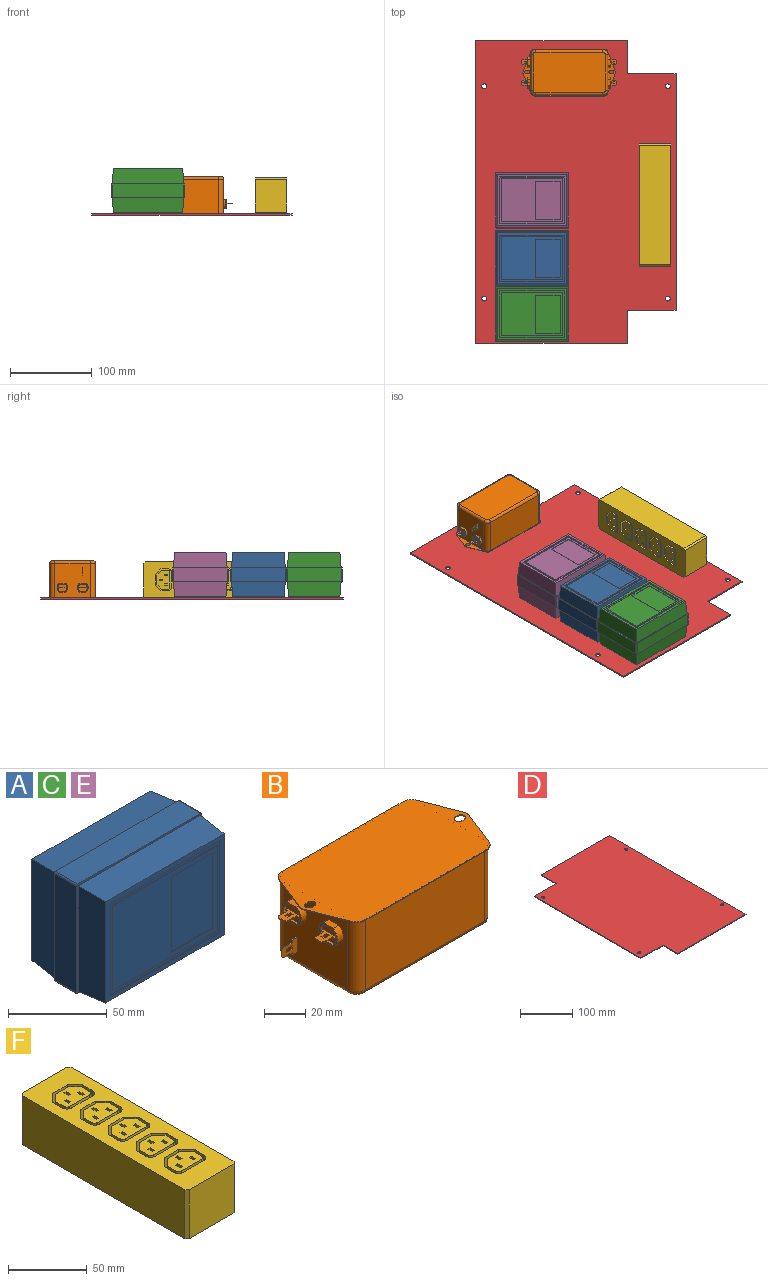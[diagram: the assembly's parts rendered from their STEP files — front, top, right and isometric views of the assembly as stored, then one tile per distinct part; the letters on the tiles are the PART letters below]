
ASSEMBLY  parts=6 mates=7
PART A: 47 faces, bbox 90x55x68 mm
  f0: plane 84.83x62.83mm, normal (0,-1,0), area 849.9mm2, adj f1,f2,f3,f4,f35,f36,f37,f38
  f1: plane 65.74x18.5mm, normal (-1,-0.08,0), area 1192.9mm2, adj f0,f2,f4,f9
  f2: plane 87.74x18.5mm, normal (0,-0.08,-1), area 1601.2mm2, adj f0,f1,f3,f9
  f3: plane 65.74x18.5mm, normal (1,-0.08,0), area 1192.9mm2, adj f0,f2,f4,f9
  f4: plane 87.74x18.5mm, normal (0,-0.08,1), area 1601.2mm2, adj f0,f1,f3,f9
  f5: plane 66x16mm, normal (-1,0,0), area 1056mm2, adj f9,f10,f16,f19
  f6: plane 88x16mm, normal (0,0,-1), area 1408mm2, adj f9,f10,f16,f17
  f7: plane 66x16mm, normal (1,0,0), area 1056mm2, adj f9,f10,f17,f18
  f8: plane 88x16mm, normal (0,0,1), area 1408mm2, adj f9,f10,f18,f19
  f9: plane 90x68mm, normal (0,-1,0), area 351mm2, adj f1,f2,f3,f4,f5,f6,f7,f8
  f10: plane 90x68mm, normal (0,1,0), area 351mm2, adj f5,f6,f7,f8,f12,f13,f14,f15
  f11: plane 84.83x62.83mm, normal (0,1,0), area 5128.6mm2, adj f12,f13,f14,f15,f20,f22,f24,f26
  f12: plane 65.74x18.5mm, normal (-1,0.08,0), area 1192.9mm2, adj f10,f11,f13,f15
  f13: plane 87.74x18.5mm, normal (0,0.08,-1), area 1601.2mm2, adj f10,f11,f12,f14
  f14: plane 65.74x18.5mm, normal (1,0.08,0), area 1192.9mm2, adj f10,f11,f13,f15
  f15: plane 87.74x18.5mm, normal (0,0.08,1), area 1601.2mm2, adj f10,f11,f12,f14
  f16: cylinder r=1mm len=16mm, axis (0,-1,0), area 25.1mm2, adj f5,f6,f9,f10
  f17: cylinder r=1mm len=16mm, axis (0,1,0), area 25.1mm2, adj f6,f7,f9,f10
  f18: cylinder r=1mm len=16mm, axis (0,-1,0), area 25.1mm2, adj f7,f8,f9,f10
  f19: cylinder r=1mm len=16mm, axis (0,1,0), area 25.1mm2, adj f5,f8,f9,f10
  f20: cylinder r=4mm len=8mm, axis (0,-1,0), area 36.7mm2, adj f11,f31
  f21: plane 6.92x6.92mm, normal (0,1,0), area 37.6mm2, adj f31
  f22: cylinder r=4mm len=8mm, axis (0,-1,0), area 36.7mm2, adj f11,f30
  f23: plane 6.92x6.92mm, normal (0,1,0), area 37.6mm2, adj f30
  f24: cylinder r=4mm len=8mm, axis (0,-1,0), area 36.7mm2, adj f11,f29
  f25: plane 6.92x6.92mm, normal (0,1,0), area 37.6mm2, adj f29
  f26: cylinder r=4mm len=8mm, axis (0,-1,0), area 36.7mm2, adj f11,f28
  f27: plane 6.92x6.92mm, normal (0,1,0), area 37.6mm2, adj f28
  f28: cone r=3.46mm half-angle=45deg, axis (0,-1,0), area 17.9mm2, adj f26,f27
  f29: cone r=3.46mm half-angle=45deg, axis (0,-1,0), area 17.9mm2, adj f24,f25
  f30: cone r=3.46mm half-angle=45deg, axis (0,-1,0), area 17.9mm2, adj f22,f23
  f31: cone r=3.46mm half-angle=45deg, axis (0,-1,0), area 17.9mm2, adj f20,f21
  f32: plane 52.83x0.5mm, normal (-1,0,0), area 26.4mm2, adj f33,f39,f40,f41
  f33: plane 74.83x0.5mm, normal (0,0,1), area 37.4mm2, adj f32,f34,f40,f41
  f34: plane 52.83x0.5mm, normal (1,0,0), area 26.4mm2, adj f33,f39,f40,f41
  f35: plane 78.83x0.5mm, normal (0,0,1), area 39.4mm2, adj f0,f36,f38,f40
  f36: plane 56.83x0.5mm, normal (-1,0,0), area 28.4mm2, adj f0,f35,f37,f40
  f37: plane 78.83x0.5mm, normal (0,0,-1), area 39.4mm2, adj f0,f36,f38,f40
  f38: plane 56.83x0.5mm, normal (1,0,0), area 28.4mm2, adj f0,f35,f37,f40
  f39: plane 74.83x0.5mm, normal (0,0,-1), area 37.4mm2, adj f32,f34,f40,f41
  f40: plane 78.83x56.83mm, normal (0,-1,0), area 526.6mm2, adj f32,f33,f34,f35,f36,f37,f38,f39
  f41: plane 74.83x52.83mm, normal (0,-1,0), area 2548.3mm2, adj f32,f33,f34,f39,f42,f43,f44,f45
  f42: plane 46.83x0.5mm, normal (-1,0,0), area 23.4mm2, adj f41,f43,f45,f46
  f43: plane 30x0.5mm, normal (0,0,-1), area 15mm2, adj f41,f42,f44,f46
  f44: plane 46.83x0.5mm, normal (1,0,0), area 23.4mm2, adj f41,f43,f45,f46
  f45: plane 30x0.5mm, normal (0,0,1), area 15mm2, adj f41,f42,f44,f46
  f46: plane 46.83x30mm, normal (0,-1,0), area 1404.9mm2, adj f42,f43,f44,f45
PART B: 154 faces, bbox 116x57.5x45.4 mm
  f0: plane 1.5x0.5mm, normal (0,-1,0), area 0.8mm2, adj f6,f7,f128,f148
  f1: plane 1.5x0.5mm, normal (0,1,0), area 0.8mm2, adj f6,f7,f128,f146
  f2: plane 4x0.5mm, normal (1,0,0), area 2mm2, adj f6,f7,f152,f153
  f3: plane 1.5x0.5mm, normal (0,-1,0), area 0.8mm2, adj f8,f9,f133,f145
  f4: plane 1.5x0.5mm, normal (0,1,0), area 0.8mm2, adj f8,f9,f133,f143
  f5: plane 4x0.5mm, normal (1,0,0), area 2mm2, adj f8,f9,f150,f151
  f6: plane 9x8.5mm, normal (0,0,1), area 46.5mm2, adj f0,f1,f2,f128,f138,f139,f140,f141
  f7: plane 9x8.5mm, normal (0,0,-1), area 46.5mm2, adj f0,f1,f2,f128,f138,f139,f140,f141
  f8: plane 9x8.5mm, normal (0,0,1), area 46.5mm2, adj f3,f4,f5,f133,f134,f135,f136,f137
  f9: plane 9x8.5mm, normal (0,0,-1), area 46.5mm2, adj f3,f4,f5,f133,f134,f135,f136,f137
  f10: plane 13x11mm, normal (1,0,0), area 36.9mm2, adj f115,f116,f117,f118,f129,f130,f131,f132
  f11: plane 44x42mm, normal (1,0,0), area 1601.3mm2, adj f22,f44,f49,f57,f115,f116,f117,f118
  f12: plane 4x0.5mm, normal (-1,0,0), area 2mm2, adj f13,f14,f109,f110
  f13: plane 11x9mm, normal (0,1,0), area 69mm2, adj f12,f21,f83,f84,f101,f102,f103,f104
  f14: plane 11x9mm, normal (0,-1,0), area 69mm2, adj f12,f21,f83,f84,f101,f102,f103,f104
  f15: plane 4x0.5mm, normal (-1,0,0), area 2mm2, adj f17,f18,f113,f114
  f16: plane 4x0.5mm, normal (-1,0,0), area 2mm2, adj f19,f20,f111,f112
  f17: plane 9x8.5mm, normal (0,0,1), area 46.5mm2, adj f15,f73,f79,f80,f89,f90,f91,f92
  f18: plane 9x8.5mm, normal (0,0,-1), area 46.5mm2, adj f15,f73,f79,f80,f89,f90,f91,f92
  f19: plane 9x8.5mm, normal (0,0,1), area 46.5mm2, adj f16,f78,f81,f82,f85,f86,f87,f88
  f20: plane 9x8.5mm, normal (0,0,-1), area 46.5mm2, adj f16,f78,f81,f82,f85,f86,f87,f88
  f21: plane 44x42mm, normal (-1,0,0), area 1596.8mm2, adj f13,f14,f22,f46,f47,f52,f59,f60
  f22: plane 113.52x57.5mm, normal (0,0,-1), area 628.3mm2, adj f11,f21,f24,f25,f26,f27,f28,f29
  f23: plane 113.52x57.5mm, normal (0,0,1), area 5861.4mm2, adj f24,f25,f26,f27,f28,f29,f30,f31
  f24: cylinder r=4.4mm len=3.2mm, axis (0,0,-1), area 1.3mm2, adj f22,f23,f25,f35
  f25: plane 23.33x9.12mm, normal (-0.93,-0.36,0), area 10mm2, adj f22,f23,f24,f26
  f26: cylinder r=6mm len=5.5mm, axis (0,0,-1), area 2.8mm2, adj f22,f23,f25,f27
  f27: plane 83.68x0.4mm, normal (0,-1,0), area 33.5mm2, adj f22,f23,f26,f28
  f28: cylinder r=6mm len=5.5mm, axis (0,0,-1), area 2.8mm2, adj f22,f23,f27,f29
  f29: plane 23.33x9.12mm, normal (0.93,-0.36,0), area 10mm2, adj f22,f23,f28,f30
  f30: cylinder r=4.4mm len=3.2mm, axis (0,0,-1), area 1.3mm2, adj f22,f23,f29,f31
  f31: plane 23.33x9.12mm, normal (0.93,0.36,0), area 10mm2, adj f22,f23,f30,f32
  f32: cylinder r=6mm len=5.5mm, axis (0,0,-1), area 2.8mm2, adj f22,f23,f31,f33
  f33: plane 83.68x0.4mm, normal (0,1,0), area 33.5mm2, adj f22,f23,f32,f34
  f34: cylinder r=6mm len=5.5mm, axis (0,0,-1), area 2.8mm2, adj f22,f23,f33,f35
  f35: plane 23.33x9.12mm, normal (-0.93,0.36,0), area 10mm2, adj f22,f23,f24,f34
  f36: plane 1.6x0.4mm, normal (0,-1,0), area 0.6mm2, adj f22,f23,f37,f38
  f37: cylinder r=2.2mm len=4.4mm, axis (0,0,1), area 2.8mm2, adj f22,f23,f36,f39
  f38: cylinder r=2.2mm len=4.4mm, axis (0,0,1), area 2.8mm2, adj f22,f23,f36,f39
  f39: plane 1.6x0.4mm, normal (0,1,0), area 0.6mm2, adj f22,f23,f37,f38
  f40: plane 1.6x0.4mm, normal (0,-1,0), area 0.6mm2, adj f22,f23,f41,f42
  f41: cylinder r=2.2mm len=4.4mm, axis (0,0,1), area 2.8mm2, adj f22,f23,f40,f43
  f42: cylinder r=2.2mm len=4.4mm, axis (0,0,1), area 2.8mm2, adj f22,f23,f40,f43
  f43: plane 1.6x0.4mm, normal (0,1,0), area 0.6mm2, adj f22,f23,f41,f42
  f44: cylinder r=6mm len=42mm, axis (0,0,1), area 395.8mm2, adj f11,f22,f45,f55
  f45: plane 82x42mm, normal (0,1,0), area 3444mm2, adj f22,f44,f46,f53
  f46: cylinder r=6mm len=42mm, axis (0,0,1), area 395.8mm2, adj f21,f22,f45,f51
  f47: cylinder r=6mm len=42mm, axis (0,0,1), area 395.8mm2, adj f21,f22,f48,f54
  f48: plane 82x42mm, normal (0,-1,0), area 3444mm2, adj f22,f47,f49,f56
  f49: cylinder r=6mm len=42mm, axis (0,0,1), area 395.8mm2, adj f11,f22,f48,f58
  f50: plane 88x50mm, normal (0,0,-1), area 4392.3mm2, adj f51,f52,f53,f54,f55,f56,f57,f58
  f51: torus R=3mm, axis (0,0,1), area 36.3mm2, adj f46,f50,f52,f53
  f52: cylinder r=3mm len=44mm, axis (0,1,0), area 207.3mm2, adj f21,f50,f51,f54
  f53: cylinder r=3mm len=82mm, axis (1,0,0), area 386.4mm2, adj f45,f50,f51,f55
  f54: torus R=3mm, axis (0,0,1), area 36.3mm2, adj f47,f50,f52,f56
  f55: torus R=3mm, axis (0,0,1), area 36.3mm2, adj f44,f50,f53,f57
  f56: cylinder r=3mm len=82mm, axis (-1,0,0), area 386.4mm2, adj f48,f50,f54,f58
  f57: cylinder r=3mm len=44mm, axis (0,-1,0), area 207.3mm2, adj f11,f50,f55,f58
  f58: torus R=3mm, axis (0,0,1), area 36.3mm2, adj f49,f50,f56,f57
  f59: cylinder r=6.5mm len=11mm, axis (1,0,0), area 52.5mm2, adj f21,f60,f62,f63
  f60: plane 6.93x4mm, normal (0,0,-1), area 27.7mm2, adj f21,f59,f61,f63
  f61: cylinder r=6.5mm len=11mm, axis (1,0,0), area 52.5mm2, adj f21,f60,f62,f63
  f62: plane 6.93x4mm, normal (0,0,1), area 27.7mm2, adj f21,f59,f61,f63
  f63: plane 13x11mm, normal (-1,0,0), area 36.9mm2, adj f59,f60,f61,f62,f74,f75,f76,f77
  f64: plane 6.93x4mm, normal (0,0,1), area 27.7mm2, adj f21,f65,f67,f68
  f65: cylinder r=6.5mm len=11mm, axis (1,0,0), area 52.5mm2, adj f21,f64,f66,f68
  f66: plane 6.93x4mm, normal (0,0,-1), area 27.7mm2, adj f21,f65,f67,f68
  f67: cylinder r=6.5mm len=11mm, axis (1,0,0), area 52.5mm2, adj f21,f64,f66,f68
  f68: plane 13x11mm, normal (-1,0,0), area 36.9mm2, adj f64,f65,f66,f67,f69,f70,f71,f72
  f69: plane 6.32x1.5mm, normal (0,0,-1), area 9.5mm2, adj f68,f70,f72,f73
  f70: cylinder r=5.5mm len=9mm, axis (-1,0,0), area 15.8mm2, adj f68,f69,f71,f73
  f71: plane 6.32x1.5mm, normal (0,0,1), area 9.5mm2, adj f68,f70,f72,f73
  f72: cylinder r=5.5mm len=9mm, axis (-1,0,0), area 15.8mm2, adj f68,f69,f71,f73
  f73: plane 11x9mm, normal (-1,0,0), area 81.9mm2, adj f17,f18,f69,f70,f71,f72,f79,f80
  f74: cylinder r=5.5mm len=9mm, axis (-1,0,0), area 15.8mm2, adj f63,f75,f77,f78
  f75: plane 6.32x1.5mm, normal (0,0,1), area 9.5mm2, adj f63,f74,f76,f78
  f76: cylinder r=5.5mm len=9mm, axis (-1,0,0), area 15.8mm2, adj f63,f75,f77,f78
  f77: plane 6.32x1.5mm, normal (0,0,-1), area 9.5mm2, adj f63,f74,f76,f78
  f78: plane 11x9mm, normal (-1,0,0), area 81.9mm2, adj f19,f20,f74,f75,f76,f77,f81,f82
  f79: plane 1.5x0.5mm, normal (0,1,0), area 0.8mm2, adj f17,f18,f73,f99
  f80: plane 1.5x0.5mm, normal (0,-1,0), area 0.8mm2, adj f17,f18,f73,f97
  f81: plane 1.5x0.5mm, normal (0,1,0), area 0.8mm2, adj f19,f20,f78,f96
  f82: plane 1.5x0.5mm, normal (0,-1,0), area 0.8mm2, adj f19,f20,f78,f94
  f83: plane 4x0.5mm, normal (0,0,-1), area 2mm2, adj f13,f14,f21,f107
  f84: plane 4x0.5mm, normal (0,0,1), area 2mm2, adj f13,f14,f21,f105
  f85: plane 2x0.5mm, normal (-1,0,0), area 1mm2, adj f19,f20,f86,f87
  f86: plane 4x0.5mm, normal (0,-1,0), area 2mm2, adj f19,f20,f85,f88
  f87: plane 4x0.5mm, normal (0,1,0), area 2mm2, adj f19,f20,f85,f88
  f88: plane 2x0.5mm, normal (1,0,0), area 1mm2, adj f19,f20,f86,f87
  f89: plane 2x0.5mm, normal (-1,0,0), area 1mm2, adj f17,f18,f90,f91
  f90: plane 4x0.5mm, normal (0,-1,0), area 2mm2, adj f17,f18,f89,f92
  f91: plane 4x0.5mm, normal (0,1,0), area 2mm2, adj f17,f18,f89,f92
  f92: plane 2x0.5mm, normal (1,0,0), area 1mm2, adj f17,f18,f90,f91
  f93: plane 6x0.5mm, normal (0,-1,0), area 3mm2, adj f19,f20,f94,f112
  f94: plane 1.5x0.5mm, normal (-1,0,0), area 0.8mm2, adj f19,f20,f82,f93
  f95: plane 6x0.5mm, normal (0,1,0), area 3mm2, adj f19,f20,f96,f111
  f96: plane 1.5x0.5mm, normal (-1,0,0), area 0.8mm2, adj f19,f20,f81,f95
  f97: plane 1.5x0.5mm, normal (-1,0,0), area 0.8mm2, adj f17,f18,f80,f98
  f98: plane 6x0.5mm, normal (0,-1,0), area 3mm2, adj f17,f18,f97,f113
  f99: plane 1.5x0.5mm, normal (-1,0,0), area 0.8mm2, adj f17,f18,f79,f100
  f100: plane 6x0.5mm, normal (0,1,0), area 3mm2, adj f17,f18,f99,f114
  f101: plane 2x0.5mm, normal (-1,0,0), area 1mm2, adj f13,f14,f102,f104
  f102: plane 4x0.5mm, normal (0,0,1), area 2mm2, adj f13,f14,f101,f103
  f103: plane 2x0.5mm, normal (1,0,0), area 1mm2, adj f13,f14,f102,f104
  f104: plane 4x0.5mm, normal (0,0,-1), area 2mm2, adj f13,f14,f101,f103
  f105: plane 1.5x0.5mm, normal (-1,0,0), area 0.8mm2, adj f13,f14,f84,f106
  f106: plane 6x0.5mm, normal (0,0,1), area 3mm2, adj f13,f14,f105,f109
  f107: plane 1.5x0.5mm, normal (-1,0,0), area 0.7mm2, adj f13,f14,f83,f108
  f108: plane 6x0.5mm, normal (0,0,-1), area 3mm2, adj f13,f14,f107,f110
  f109: plane 1x1mm, normal (-0.71,0,0.71), area 0.7mm2, adj f12,f13,f14,f106
  f110: plane 1x1mm, normal (-0.71,0,-0.71), area 0.7mm2, adj f12,f13,f14,f108
  f111: plane 1x1mm, normal (-0.71,0.71,0), area 0.7mm2, adj f16,f19,f20,f95
  f112: plane 1x1mm, normal (-0.71,-0.71,0), area 0.7mm2, adj f16,f19,f20,f93
  f113: plane 1x1mm, normal (-0.71,-0.71,0), area 0.7mm2, adj f15,f17,f18,f98
  f114: plane 1x1mm, normal (-0.71,0.71,0), area 0.7mm2, adj f15,f17,f18,f100
  f115: cylinder r=6.5mm len=11mm, axis (-1,0,0), area 52.5mm2, adj f10,f11,f116,f118
  f116: plane 6.93x4mm, normal (0,0,1), area 27.7mm2, adj f10,f11,f115,f117
  f117: cylinder r=6.5mm len=11mm, axis (-1,0,0), area 52.5mm2, adj f10,f11,f116,f118
  f118: plane 6.93x4mm, normal (0,0,-1), area 27.7mm2, adj f10,f11,f115,f117
  f119: plane 6.93x4mm, normal (0,0,-1), area 27.7mm2, adj f11,f120,f122,f123
  f120: cylinder r=6.5mm len=11mm, axis (-1,0,0), area 52.5mm2, adj f11,f119,f121,f123
  f121: plane 6.93x4mm, normal (0,0,1), area 27.7mm2, adj f11,f120,f122,f123
  f122: cylinder r=6.5mm len=11mm, axis (-1,0,0), area 52.5mm2, adj f11,f119,f121,f123
  f123: plane 13x11mm, normal (1,0,0), area 36.9mm2, adj f119,f120,f121,f122,f124,f125,f126,f127
  f124: plane 6.32x1.5mm, normal (0,0,-1), area 9.5mm2, adj f123,f125,f127,f128
  f125: cylinder r=5.5mm len=9mm, axis (1,0,0), area 15.8mm2, adj f123,f124,f126,f128
  f126: plane 6.32x1.5mm, normal (0,0,1), area 9.5mm2, adj f123,f125,f127,f128
  f127: cylinder r=5.5mm len=9mm, axis (1,0,0), area 15.8mm2, adj f123,f124,f126,f128
  f128: plane 11x9mm, normal (1,0,0), area 81.9mm2, adj f0,f1,f6,f7,f124,f125,f126,f127
  f129: cylinder r=5.5mm len=9mm, axis (1,0,0), area 15.8mm2, adj f10,f130,f132,f133
  f130: plane 6.32x1.5mm, normal (0,0,1), area 9.5mm2, adj f10,f129,f131,f133
  f131: cylinder r=5.5mm len=9mm, axis (1,0,0), area 15.8mm2, adj f10,f130,f132,f133
  f132: plane 6.32x1.5mm, normal (0,0,-1), area 9.5mm2, adj f10,f129,f131,f133
  f133: plane 11x9mm, normal (1,0,0), area 81.9mm2, adj f3,f4,f8,f9,f129,f130,f131,f132
  f134: plane 2x0.5mm, normal (-1,0,0), area 1mm2, adj f8,f9,f135,f136
  f135: plane 4x0.5mm, normal (0,-1,0), area 2mm2, adj f8,f9,f134,f137
  f136: plane 4x0.5mm, normal (0,1,0), area 2mm2, adj f8,f9,f134,f137
  f137: plane 2x0.5mm, normal (1,0,0), area 1mm2, adj f8,f9,f135,f136
  f138: plane 2x0.5mm, normal (1,0,0), area 1mm2, adj f6,f7,f139,f140
  f139: plane 4x0.5mm, normal (0,1,0), area 2mm2, adj f6,f7,f138,f141
  f140: plane 4x0.5mm, normal (0,-1,0), area 2mm2, adj f6,f7,f138,f141
  f141: plane 2x0.5mm, normal (-1,0,0), area 1mm2, adj f6,f7,f139,f140
  f142: plane 6x0.5mm, normal (0,1,0), area 3mm2, adj f8,f9,f143,f151
  f143: plane 1.5x0.5mm, normal (1,0,0), area 0.8mm2, adj f4,f8,f9,f142
  f144: plane 6x0.5mm, normal (0,-1,0), area 3mm2, adj f8,f9,f145,f150
  f145: plane 1.5x0.5mm, normal (1,0,0), area 0.8mm2, adj f3,f8,f9,f144
  f146: plane 1.5x0.5mm, normal (1,0,0), area 0.8mm2, adj f1,f6,f7,f147
  f147: plane 6x0.5mm, normal (0,1,0), area 3mm2, adj f6,f7,f146,f153
  f148: plane 1.5x0.5mm, normal (1,0,0), area 0.8mm2, adj f0,f6,f7,f149
  f149: plane 6x0.5mm, normal (0,-1,0), area 3mm2, adj f6,f7,f148,f152
  f150: plane 1x1mm, normal (0.71,-0.71,0), area 0.7mm2, adj f5,f8,f9,f144
  f151: plane 1x1mm, normal (0.71,0.71,0), area 0.7mm2, adj f5,f8,f9,f142
  f152: plane 1x1mm, normal (0.71,-0.71,0), area 0.7mm2, adj f2,f6,f7,f149
  f153: plane 1x1mm, normal (0.71,0.71,0), area 0.7mm2, adj f2,f6,f7,f147
PART C: same geometry as A
PART D: 14 faces, bbox 245x370x1.6 mm
  f0: plane 290x1.6mm, normal (-1,0,0), area 464mm2, adj f3,f4,f10,f13
  f1: plane 185x1.6mm, normal (0,-1,0), area 296mm2, adj f3,f4,f5,f9
  f2: plane 185x1.6mm, normal (0,1,0), area 296mm2, adj f3,f4,f5,f12
  f3: plane 370x245mm, normal (0,0,1), area 85736.9mm2, adj f0,f1,f2,f5,f6,f7,f8,f9
  f4: plane 370x245mm, normal (0,0,-1), area 85736.9mm2, adj f0,f1,f2,f5,f6,f7,f8,f9
  f5: plane 370x1.6mm, normal (1,0,0), area 592mm2, adj f1,f2,f3,f4
  f6: cylinder r=3mm len=6mm, axis (0,0,1), area 30.2mm2, adj f3,f4
  f7: cylinder r=3mm len=6mm, axis (0,0,1), area 30.2mm2, adj f3,f4
  f8: cylinder r=3mm len=6mm, axis (0,0,1), area 30.2mm2, adj f3,f4
  f9: plane 40x1.6mm, normal (-1,0,0), area 64mm2, adj f1,f3,f4,f10
  f10: plane 60x1.6mm, normal (0,-1,0), area 96mm2, adj f0,f3,f4,f9
  f11: cylinder r=3mm len=6mm, axis (0,0,1), area 30.2mm2, adj f3,f4
  f12: plane 40x1.6mm, normal (-1,0,0), area 64mm2, adj f2,f3,f4,f13
  f13: plane 60x1.6mm, normal (0,1,0), area 96mm2, adj f0,f3,f4,f12
PART E: same geometry as A
PART F: 175 faces, bbox 44x150x38 mm
  f0: plane 150x44mm, normal (0,0,1), area 4194.1mm2, adj f1,f2,f3,f4,f6,f7,f8,f9
  f1: plane 40x38mm, normal (0,-1,0), area 1520mm2, adj f0,f5,f171,f174
  f2: plane 146x38mm, normal (1,0,0), area 5548mm2, adj f0,f5,f171,f172
  f3: plane 40x38mm, normal (0,1,0), area 1520mm2, adj f0,f5,f172,f173
  f4: plane 146x38mm, normal (-1,0,0), area 5548mm2, adj f0,f5,f173,f174
  f5: plane 150x44mm, normal (0,0,-1), area 6592mm2, adj f1,f2,f3,f4,f171,f172,f173,f174
  f6: plane 18.7x18.16mm, normal (0,1,0), area 339.5mm2, adj f0,f7,f21,f22
  f7: cylinder r=4.42mm len=18.7mm, axis (0,0,1), area 129.9mm2, adj f0,f6,f8,f22
  f8: plane 18.7x8.55mm, normal (-1,0,0), area 159.9mm2, adj f0,f7,f9,f22
  f9: plane 18.7x6.83mm, normal (-0.71,-0.71,0), area 180.6mm2, adj f0,f8,f10,f22
  f10: plane 18.7x13.34mm, normal (0,-1,0), area 249.5mm2, adj f0,f9,f11,f22
  f11: plane 18.7x6.83mm, normal (0.71,-0.71,0), area 180.6mm2, adj f0,f10,f12,f22
  f12: plane 18.7x8.55mm, normal (1,0,0), area 159.9mm2, adj f0,f11,f21,f22
  f13: plane 18.7x18.16mm, normal (0,-1,0), area 339.5mm2, adj f14,f20,f22,f23
  f14: cylinder r=2.42mm len=18.7mm, axis (0,0,1), area 71.1mm2, adj f13,f15,f22,f23
  f15: plane 18.7x7.72mm, normal (-1,0,0), area 144.4mm2, adj f14,f16,f22,f23
  f16: plane 18.7x5.66mm, normal (-0.71,0.71,0), area 149.6mm2, adj f15,f17,f22,f23
  f17: plane 18.7x11.69mm, normal (0,1,0), area 218.5mm2, adj f16,f18,f22,f23
  f18: plane 18.7x5.66mm, normal (0.71,0.71,0), area 149.6mm2, adj f17,f19,f22,f23
  f19: plane 18.7x7.72mm, normal (1,0,0), area 144.4mm2, adj f18,f20,f22,f23
  f20: cylinder r=2.42mm len=18.7mm, axis (0,0,1), area 71.1mm2, adj f13,f19,f22,f23
  f21: cylinder r=4.42mm len=18.7mm, axis (0,0,1), area 129.9mm2, adj f0,f6,f12,f22
  f22: plane 27x19.8mm, normal (0,0,1), area 150.7mm2, adj f6,f7,f8,f9,f10,f11,f12,f13
  f23: plane 23x15.8mm, normal (0,0,1), area 304.9mm2, adj f13,f14,f15,f16,f17,f18,f19,f20
  f24: plane 18.7x4mm, normal (-1,0,0), area 74.8mm2, adj f23,f25,f27,f28
  f25: plane 18.7x2mm, normal (0,-1,0), area 37.4mm2, adj f23,f24,f26,f28
  f26: plane 18.7x4mm, normal (1,0,0), area 74.8mm2, adj f23,f25,f27,f28
  f27: plane 18.7x2mm, normal (0,1,0), area 37.4mm2, adj f23,f24,f26,f28
  f28: plane 4x2mm, normal (0,0,1), area 8mm2, adj f24,f25,f26,f27
  f29: plane 18.7x4mm, normal (-1,0,0), area 74.8mm2, adj f23,f30,f32,f33
  f30: plane 18.7x2mm, normal (0,-1,0), area 37.4mm2, adj f23,f29,f31,f33
  f31: plane 18.7x4mm, normal (1,0,0), area 74.8mm2, adj f23,f30,f32,f33
  f32: plane 18.7x2mm, normal (0,1,0), area 37.4mm2, adj f23,f29,f31,f33
  f33: plane 4x2mm, normal (0,0,1), area 8mm2, adj f29,f30,f31,f32
  f34: plane 18.7x4mm, normal (1,0,0), area 74.8mm2, adj f23,f35,f37,f38
  f35: plane 18.7x2mm, normal (0,1,0), area 37.4mm2, adj f23,f34,f36,f38
  f36: plane 18.7x4mm, normal (-1,0,0), area 74.8mm2, adj f23,f35,f37,f38
  f37: plane 18.7x2mm, normal (0,-1,0), area 37.4mm2, adj f23,f34,f36,f38
  f38: plane 4x2mm, normal (0,0,1), area 8mm2, adj f34,f35,f36,f37
  f39: plane 18.7x18.16mm, normal (0,-1,0), area 339.5mm2, adj f40,f54,f55,f107
  f40: cylinder r=2.42mm len=18.7mm, axis (0,0,1), area 71.1mm2, adj f39,f41,f55,f107
  f41: plane 18.7x7.72mm, normal (-1,0,0), area 144.4mm2, adj f40,f42,f55,f107
  f42: plane 18.7x5.66mm, normal (-0.71,0.71,0), area 149.6mm2, adj f41,f43,f55,f107
  f43: plane 18.7x11.69mm, normal (0,1,0), area 218.5mm2, adj f42,f44,f55,f107
  f44: plane 18.7x5.66mm, normal (0.71,0.71,0), area 149.6mm2, adj f43,f45,f55,f107
  f45: plane 18.7x7.72mm, normal (1,0,0), area 144.4mm2, adj f44,f54,f55,f107
  f46: plane 18.7x18.16mm, normal (0,1,0), area 339.5mm2, adj f0,f47,f53,f55
  f47: cylinder r=4.42mm len=18.7mm, axis (0,0,1), area 129.9mm2, adj f0,f46,f48,f55
  f48: plane 18.7x8.55mm, normal (-1,0,0), area 159.9mm2, adj f0,f47,f49,f55
  f49: plane 18.7x6.83mm, normal (-0.71,-0.71,0), area 180.6mm2, adj f0,f48,f50,f55
  f50: plane 18.7x13.34mm, normal (0,-1,0), area 249.5mm2, adj f0,f49,f51,f55
  f51: plane 18.7x6.83mm, normal (0.71,-0.71,0), area 180.6mm2, adj f0,f50,f52,f55
  f52: plane 18.7x8.55mm, normal (1,0,0), area 159.9mm2, adj f0,f51,f53,f55
  f53: cylinder r=4.42mm len=18.7mm, axis (0,0,1), area 129.9mm2, adj f0,f46,f52,f55
  f54: cylinder r=2.42mm len=18.7mm, axis (0,0,1), area 71.1mm2, adj f39,f45,f55,f107
  f55: plane 27x19.8mm, normal (0,0,1), area 150.7mm2, adj f39,f40,f41,f42,f43,f44,f45,f46
  f56: plane 18.7x18.16mm, normal (0,-1,0), area 339.5mm2, adj f57,f71,f72,f129
  f57: cylinder r=2.42mm len=18.7mm, axis (0,0,1), area 71.1mm2, adj f56,f58,f72,f129
  f58: plane 18.7x7.72mm, normal (-1,0,0), area 144.4mm2, adj f57,f59,f72,f129
  f59: plane 18.7x5.66mm, normal (-0.71,0.71,0), area 149.6mm2, adj f58,f60,f72,f129
  f60: plane 18.7x11.69mm, normal (0,1,0), area 218.5mm2, adj f59,f61,f72,f129
  f61: plane 18.7x5.66mm, normal (0.71,0.71,0), area 149.6mm2, adj f60,f62,f72,f129
  f62: plane 18.7x7.72mm, normal (1,0,0), area 144.4mm2, adj f61,f71,f72,f129
  f63: plane 18.7x18.16mm, normal (0,1,0), area 339.5mm2, adj f0,f64,f70,f72
  f64: cylinder r=4.42mm len=18.7mm, axis (0,0,1), area 129.9mm2, adj f0,f63,f65,f72
  f65: plane 18.7x8.55mm, normal (-1,0,0), area 159.9mm2, adj f0,f64,f66,f72
  f66: plane 18.7x6.83mm, normal (-0.71,-0.71,0), area 180.6mm2, adj f0,f65,f67,f72
  f67: plane 18.7x13.34mm, normal (0,-1,0), area 249.5mm2, adj f0,f66,f68,f72
  f68: plane 18.7x6.83mm, normal (0.71,-0.71,0), area 180.6mm2, adj f0,f67,f69,f72
  f69: plane 18.7x8.55mm, normal (1,0,0), area 159.9mm2, adj f0,f68,f70,f72
  f70: cylinder r=4.42mm len=18.7mm, axis (0,0,1), area 129.9mm2, adj f0,f63,f69,f72
  f71: cylinder r=2.42mm len=18.7mm, axis (0,0,1), area 71.1mm2, adj f56,f62,f72,f129
  f72: plane 27x19.8mm, normal (0,0,1), area 150.7mm2, adj f56,f57,f58,f59,f60,f61,f62,f63
  f73: plane 18.7x18.16mm, normal (0,-1,0), area 339.5mm2, adj f74,f88,f89,f130
  f74: cylinder r=2.42mm len=18.7mm, axis (0,0,1), area 71.1mm2, adj f73,f75,f89,f130
  f75: plane 18.7x7.72mm, normal (-1,0,0), area 144.4mm2, adj f74,f76,f89,f130
  f76: plane 18.7x5.66mm, normal (-0.71,0.71,0), area 149.6mm2, adj f75,f77,f89,f130
  f77: plane 18.7x11.69mm, normal (0,1,0), area 218.5mm2, adj f76,f78,f89,f130
  f78: plane 18.7x5.66mm, normal (0.71,0.71,0), area 149.6mm2, adj f77,f79,f89,f130
  f79: plane 18.7x7.72mm, normal (1,0,0), area 144.4mm2, adj f78,f88,f89,f130
  f80: plane 18.7x18.16mm, normal (0,1,0), area 339.5mm2, adj f0,f81,f87,f89
  f81: cylinder r=4.42mm len=18.7mm, axis (0,0,1), area 129.9mm2, adj f0,f80,f82,f89
  f82: plane 18.7x8.55mm, normal (-1,0,0), area 159.9mm2, adj f0,f81,f83,f89
  f83: plane 18.7x6.83mm, normal (-0.71,-0.71,0), area 180.6mm2, adj f0,f82,f84,f89
  f84: plane 18.7x13.34mm, normal (0,-1,0), area 249.5mm2, adj f0,f83,f85,f89
  f85: plane 18.7x6.83mm, normal (0.71,-0.71,0), area 180.6mm2, adj f0,f84,f86,f89
  f86: plane 18.7x8.55mm, normal (1,0,0), area 159.9mm2, adj f0,f85,f87,f89
  f87: cylinder r=4.42mm len=18.7mm, axis (0,0,1), area 129.9mm2, adj f0,f80,f86,f89
  f88: cylinder r=2.42mm len=18.7mm, axis (0,0,1), area 71.1mm2, adj f73,f79,f89,f130
  f89: plane 27x19.8mm, normal (0,0,1), area 150.7mm2, adj f73,f74,f75,f76,f77,f78,f79,f80
  f90: plane 18.7x18.16mm, normal (0,-1,0), area 339.5mm2, adj f91,f105,f106,f123
  f91: cylinder r=2.42mm len=18.7mm, axis (0,0,1), area 71.1mm2, adj f90,f92,f106,f123
  f92: plane 18.7x7.72mm, normal (-1,0,0), area 144.4mm2, adj f91,f93,f106,f123
  f93: plane 18.7x5.66mm, normal (-0.71,0.71,0), area 149.6mm2, adj f92,f94,f106,f123
  f94: plane 18.7x11.69mm, normal (0,1,0), area 218.5mm2, adj f93,f95,f106,f123
  f95: plane 18.7x5.66mm, normal (0.71,0.71,0), area 149.6mm2, adj f94,f96,f106,f123
  f96: plane 18.7x7.72mm, normal (1,0,0), area 144.4mm2, adj f95,f105,f106,f123
  f97: plane 18.7x18.16mm, normal (0,1,0), area 339.5mm2, adj f0,f98,f104,f106
  f98: cylinder r=4.42mm len=18.7mm, axis (0,0,1), area 129.9mm2, adj f0,f97,f99,f106
  f99: plane 18.7x8.55mm, normal (-1,0,0), area 159.9mm2, adj f0,f98,f100,f106
  f100: plane 18.7x6.83mm, normal (-0.71,-0.71,0), area 180.6mm2, adj f0,f99,f101,f106
  f101: plane 18.7x13.34mm, normal (0,-1,0), area 249.5mm2, adj f0,f100,f102,f106
  f102: plane 18.7x6.83mm, normal (0.71,-0.71,0), area 180.6mm2, adj f0,f101,f103,f106
  f103: plane 18.7x8.55mm, normal (1,0,0), area 159.9mm2, adj f0,f102,f104,f106
  f104: cylinder r=4.42mm len=18.7mm, axis (0,0,1), area 129.9mm2, adj f0,f97,f103,f106
  f105: cylinder r=2.42mm len=18.7mm, axis (0,0,1), area 71.1mm2, adj f90,f96,f106,f123
  f106: plane 27x19.8mm, normal (0,0,1), area 150.7mm2, adj f90,f91,f92,f93,f94,f95,f96,f97
  f107: plane 23x15.8mm, normal (0,0,1), area 304.9mm2, adj f39,f40,f41,f42,f43,f44,f45,f54
  f108: plane 18.7x4mm, normal (1,0,0), area 74.8mm2, adj f107,f109,f111,f112
  f109: plane 18.7x2mm, normal (0,1,0), area 37.4mm2, adj f107,f108,f110,f112
  f110: plane 18.7x4mm, normal (-1,0,0), area 74.8mm2, adj f107,f109,f111,f112
  f111: plane 18.7x2mm, normal (0,-1,0), area 37.4mm2, adj f107,f108,f110,f112
  f112: plane 4x2mm, normal (0,0,1), area 8mm2, adj f108,f109,f110,f111
  f113: plane 18.7x2mm, normal (0,1,0), area 37.4mm2, adj f107,f114,f116,f117
  f114: plane 18.7x4mm, normal (-1,0,0), area 74.8mm2, adj f107,f113,f115,f117
  f115: plane 18.7x2mm, normal (0,-1,0), area 37.4mm2, adj f107,f114,f116,f117
  f116: plane 18.7x4mm, normal (1,0,0), area 74.8mm2, adj f107,f113,f115,f117
  f117: plane 4x2mm, normal (0,0,1), area 8mm2, adj f113,f114,f115,f116
  f118: plane 18.7x2mm, normal (0,-1,0), area 37.4mm2, adj f107,f119,f121,f122
  f119: plane 18.7x4mm, normal (1,0,0), area 74.8mm2, adj f107,f118,f120,f122
  f120: plane 18.7x2mm, normal (0,1,0), area 37.4mm2, adj f107,f119,f121,f122
  f121: plane 18.7x4mm, normal (-1,0,0), area 74.8mm2, adj f107,f118,f120,f122
  f122: plane 4x2mm, normal (0,0,1), area 8mm2, adj f118,f119,f120,f121
  f123: plane 23x15.8mm, normal (0,0,1), area 304.9mm2, adj f90,f91,f92,f93,f94,f95,f96,f105
  f124: plane 18.7x4mm, normal (1,0,0), area 74.8mm2, adj f123,f125,f127,f128
  f125: plane 18.7x2mm, normal (0,1,0), area 37.4mm2, adj f123,f124,f126,f128
  f126: plane 18.7x4mm, normal (-1,0,0), area 74.8mm2, adj f123,f125,f127,f128
  f127: plane 18.7x2mm, normal (0,-1,0), area 37.4mm2, adj f123,f124,f126,f128
  f128: plane 4x2mm, normal (0,0,1), area 8mm2, adj f124,f125,f126,f127
  f129: plane 23x15.8mm, normal (0,0,1), area 304.9mm2, adj f56,f57,f58,f59,f60,f61,f62,f71
  f130: plane 23x15.8mm, normal (0,0,1), area 304.9mm2, adj f73,f74,f75,f76,f77,f78,f79,f88
  f131: plane 18.7x2mm, normal (0,-1,0), area 37.4mm2, adj f130,f132,f134,f135
  f132: plane 18.7x4mm, normal (1,0,0), area 74.8mm2, adj f130,f131,f133,f135
  f133: plane 18.7x2mm, normal (0,1,0), area 37.4mm2, adj f130,f132,f134,f135
  f134: plane 18.7x4mm, normal (-1,0,0), area 74.8mm2, adj f130,f131,f133,f135
  f135: plane 4x2mm, normal (0,0,1), area 8mm2, adj f131,f132,f133,f134
  f136: plane 18.7x4mm, normal (1,0,0), area 74.8mm2, adj f129,f137,f139,f140
  f137: plane 18.7x2mm, normal (0,1,0), area 37.4mm2, adj f129,f136,f138,f140
  f138: plane 18.7x4mm, normal (-1,0,0), area 74.8mm2, adj f129,f137,f139,f140
  f139: plane 18.7x2mm, normal (0,-1,0), area 37.4mm2, adj f129,f136,f138,f140
  f140: plane 4x2mm, normal (0,0,1), area 8mm2, adj f136,f137,f138,f139
  f141: plane 18.7x2mm, normal (0,1,0), area 37.4mm2, adj f129,f142,f144,f145
  f142: plane 18.7x4mm, normal (-1,0,0), area 74.8mm2, adj f129,f141,f143,f145
  f143: plane 18.7x2mm, normal (0,-1,0), area 37.4mm2, adj f129,f142,f144,f145
  f144: plane 18.7x4mm, normal (1,0,0), area 74.8mm2, adj f129,f141,f143,f145
  f145: plane 4x2mm, normal (0,0,1), area 8mm2, adj f141,f142,f143,f144
  f146: plane 18.7x2mm, normal (0,-1,0), area 37.4mm2, adj f129,f147,f149,f150
  f147: plane 18.7x4mm, normal (1,0,0), area 74.8mm2, adj f129,f146,f148,f150
  f148: plane 18.7x2mm, normal (0,1,0), area 37.4mm2, adj f129,f147,f149,f150
  f149: plane 18.7x4mm, normal (-1,0,0), area 74.8mm2, adj f129,f146,f148,f150
  f150: plane 4x2mm, normal (0,0,1), area 8mm2, adj f146,f147,f148,f149
  f151: plane 18.7x4mm, normal (1,0,0), area 74.8mm2, adj f130,f152,f154,f155
  f152: plane 18.7x2mm, normal (0,1,0), area 37.4mm2, adj f130,f151,f153,f155
  f153: plane 18.7x4mm, normal (-1,0,0), area 74.8mm2, adj f130,f152,f154,f155
  f154: plane 18.7x2mm, normal (0,-1,0), area 37.4mm2, adj f130,f151,f153,f155
  f155: plane 4x2mm, normal (0,0,1), area 8mm2, adj f151,f152,f153,f154
  f156: plane 18.7x2mm, normal (0,1,0), area 37.4mm2, adj f130,f157,f159,f160
  f157: plane 18.7x4mm, normal (-1,0,0), area 74.8mm2, adj f130,f156,f158,f160
  f158: plane 18.7x2mm, normal (0,-1,0), area 37.4mm2, adj f130,f157,f159,f160
  f159: plane 18.7x4mm, normal (1,0,0), area 74.8mm2, adj f130,f156,f158,f160
  f160: plane 4x2mm, normal (0,0,1), area 8mm2, adj f156,f157,f158,f159
  f161: plane 18.7x2mm, normal (0,-1,0), area 37.4mm2, adj f123,f162,f164,f165
  f162: plane 18.7x4mm, normal (1,0,0), area 74.8mm2, adj f123,f161,f163,f165
  f163: plane 18.7x2mm, normal (0,1,0), area 37.4mm2, adj f123,f162,f164,f165
  f164: plane 18.7x4mm, normal (-1,0,0), area 74.8mm2, adj f123,f161,f163,f165
  f165: plane 4x2mm, normal (0,0,1), area 8mm2, adj f161,f162,f163,f164
  f166: plane 18.7x2mm, normal (0,1,0), area 37.4mm2, adj f123,f167,f169,f170
  f167: plane 18.7x4mm, normal (-1,0,0), area 74.8mm2, adj f123,f166,f168,f170
  f168: plane 18.7x2mm, normal (0,-1,0), area 37.4mm2, adj f123,f167,f169,f170
  f169: plane 18.7x4mm, normal (1,0,0), area 74.8mm2, adj f123,f166,f168,f170
  f170: plane 4x2mm, normal (0,0,1), area 8mm2, adj f166,f167,f168,f169
  f171: plane 38x2mm, normal (0.71,-0.71,0), area 107.5mm2, adj f0,f1,f2,f5
  f172: plane 38x2mm, normal (0.71,0.71,0), area 107.5mm2, adj f0,f2,f3,f5
  f173: plane 38x2mm, normal (-0.71,0.71,0), area 107.5mm2, adj f0,f3,f4,f5
  f174: plane 38x2mm, normal (-0.71,-0.71,0), area 107.5mm2, adj f0,f1,f4,f5
PLACE A rot(axis=(-1,0,0),90deg) t=(-93.17,-114.84,30.1)mm
PLACE B rot(axis=(-1,0,0),180deg) t=(-64.71,175.7,2)mm
PLACE C rot(axis=(-1,0,0),90deg) t=(-93.17,-183.2,30.1)mm
PLACE D rot(axis=(0,-1,0),180deg) t=(127.68,-185,1.6)mm
PLACE E rot(axis=(-1,0,0),90deg) t=(-93.17,-43.64,30.1)mm
PLACE F rot(axis=(0,-1,0),90deg) t=(120.94,-16.1,23.6)mm
MATE planar E.f7 <-> C.f7  axis (1,0,0) through (-3.67,-10.14,30.1)mm
MATE planar A.f24 <-> D.f4  axis (0,0,-1) through (-16.25,-57.33,1.6)mm
MATE planar E.f26 <-> D.f4  axis (0,0,-1) through (-16.25,-34.15,1.6)mm
MATE planar D.f4 <-> F.f4  axis (0,0,1) through (0,0,1.6)mm
MATE planar B.f23 <-> D.f4  axis (0,0,-1) through (-3.07,146.25,1.6)mm
MATE planar D.f4 <-> C.f24  axis (0,0,1) through (0,0,1.6)mm
MATE planar A.f7 <-> C.f7  axis (1,0,0) through (-3.67,-48.34,38.1)mm
